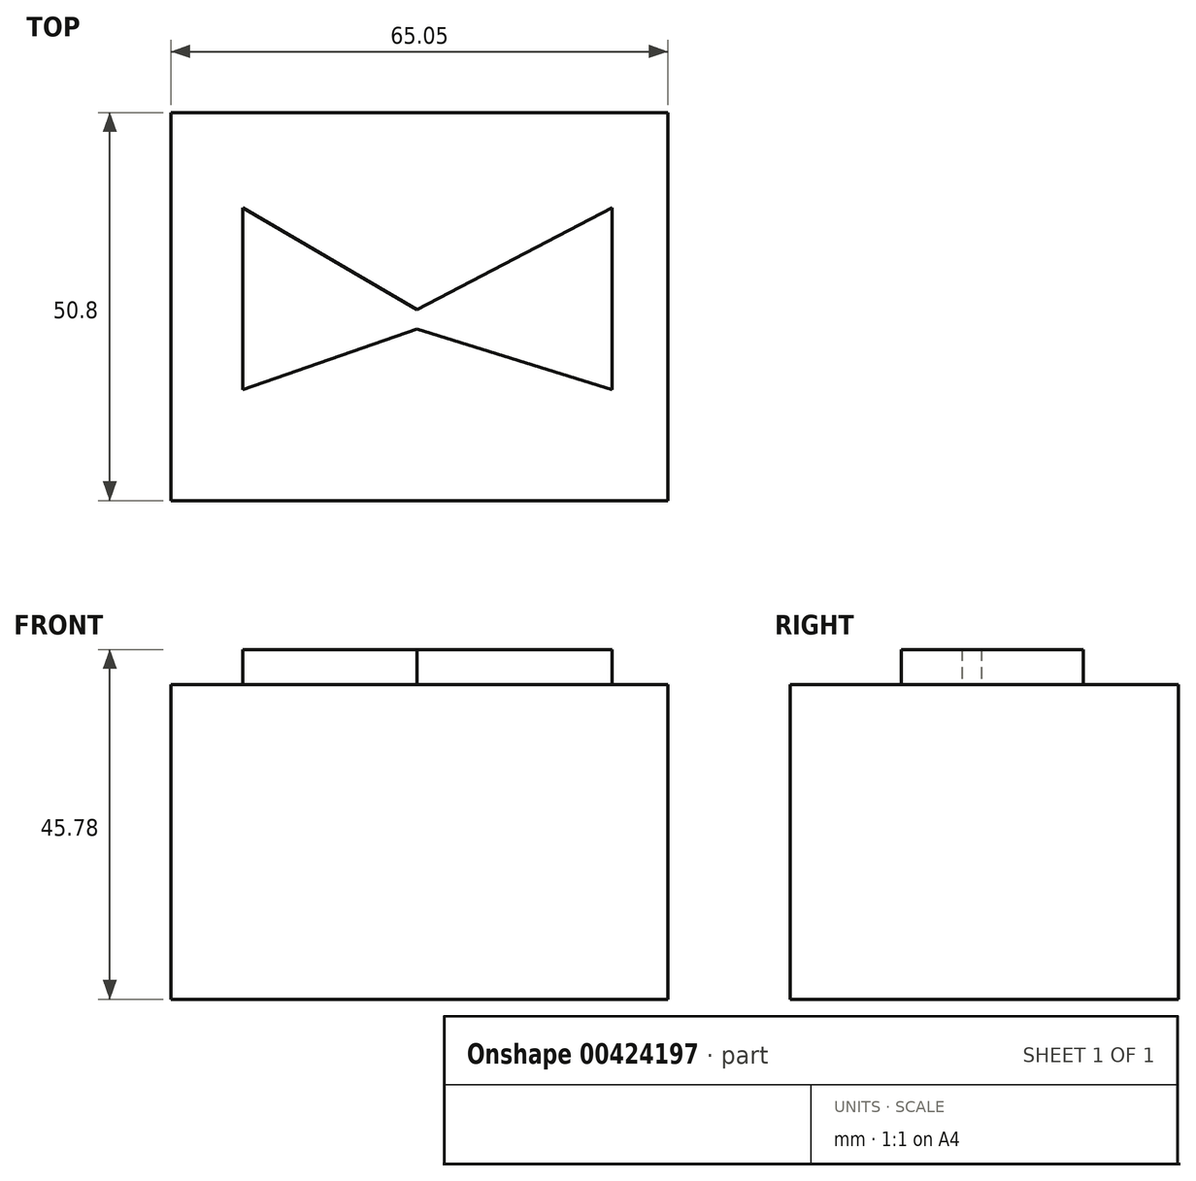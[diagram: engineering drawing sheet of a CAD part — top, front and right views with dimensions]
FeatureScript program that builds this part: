
annotation { "Feature Type Name" : "Feature", "Feature Type Description" : "" }
export const myFeature = defineFeature(function(context is Context, id is Id, definition is map)
    precondition{}
    {
        {
            var Q0;
            Q0=qCreatedBy(makeId("Front.planeOp"),FACE);
            var sketch = newSketch(context, id + "F0", { "sketchPlane" : qUnion([Q0])});
            skLineSegment(sketch, "E0.bottom", {"start": v(-32.21, 17.68) * mm, "end": v(32.84, 17.68) * mm});
            skLineSegment(sketch, "E0.top", {"start": v(-32.21, -23.53) * mm, "end": v(32.84, -23.53) * mm});
            skLineSegment(sketch, "E0.left", {"start": v(-32.21, 17.68) * mm, "end": v(-32.21, -23.53) * mm});
            skLineSegment(sketch, "E0.right", {"start": v(32.84, 17.68) * mm, "end": v(32.84, -23.53) * mm});
            skSolve(sketch);
        }
        {
            var Q0;
            Q0 = qSketchRegion(id + "F0", true);
            extrude(context, id + "F1", {"entities" : qUnion([Q0]), "depth" : 25.4 * mm});
        }
        {
            var Q0;
            Q0=makeQuery(id+"F1.opExtrude","CAP_FACE",FACE,{"disambiguationData":[OSD([sQuery(id+"F0.wireOp",EDGE,"E0.bottom"),sQuery(id+"F0.wireOp",EDGE,"E0.top"),sQuery(id+"F0.wireOp",EDGE,"E0.left"),sQuery(id+"F0.wireOp",EDGE,"E0.right")])],"isStart":false});
            var sketch = newSketch(context, id + "F2", { "sketchPlane" : qUnion([Q0])});
            skLineSegment(sketch, "E1", {"start": v(-23.43, 2.82) * mm, "end": v(-23.43, -9.1) * mm});
            skLineSegment(sketch, "E2", {"start": v(-23.43, -9.1) * mm, "end": v(0, -3.24) * mm});
            skLineSegment(sketch, "E3", {"start": v(-23.43, 2.82) * mm, "end": v(0, -3.24) * mm});
            skLineSegment(sketch, "E4", {"start": v(0, -3.24) * mm, "end": v(20.92, 2.82) * mm});
            skLineSegment(sketch, "E5", {"start": v(20.92, 2.82) * mm, "end": v(20.92, -9.1) * mm});
            skLineSegment(sketch, "E6", {"start": v(20.92, -9.1) * mm, "end": v(0, -3.24) * mm});
            skSolve(sketch);
        }
        {
            var Q0;
            Q0 = qSketchRegion(id + "F2", true);
            var Q1;
            Q1=makeQuery(id+"F2.imprint","IMPRINT",FACE,{"disambiguationData":[TD([[makeQuery(id+"F2.imprint","IMPRINT",EDGE,{"derivedFrom":sQuery(id+"F2.wireOp",EDGE,"E1")}),-1.0]])]});
            extrude(context, id + "F3", {"entities" : qUnion([Q0, Q1]), "operationType" : NewBodyOperationType.ADD, "depth" : 25.4 * mm});
        }
        {
            var Q0;
            {var subQ0=sQuery(id+"F0.wireOp",EDGE,"E0.bottom");Q0=makeQuery(id+"F3.boolean.opBoolean","MERGE",FACE,{"derivedFrom":[makeQuery(id+"F1.opExtrude","SWEPT_FACE",FACE,{"disambiguationData":[OSD([subQ0])]}),makeQuery(id+"F3.opExtrude","SWEPT_FACE",FACE,{"disambiguationData":[OSD([subQ0])]})]});}
            var sketch = newSketch(context, id + "F4", { "sketchPlane" : qUnion([Q0])});
            skLineSegment(sketch, "E7", {"start": v(-22.8, -12.45) * mm, "end": v(-22.8, -36.3) * mm});
            skLineSegment(sketch, "E8", {"start": v(25.52, -12.45) * mm, "end": v(25.52, -36.3) * mm});
            skLineSegment(sketch, "E9", {"start": v(-22.8, -12.45) * mm, "end": v(0, -25.83) * mm});
            skLineSegment(sketch, "E10", {"start": v(-22.8, -36.3) * mm, "end": v(0, -28.34) * mm});
            skLineSegment(sketch, "E11", {"start": v(0, -25.83) * mm, "end": v(25.52, -12.45) * mm});
            skLineSegment(sketch, "E12", {"start": v(0, -28.34) * mm, "end": v(25.52, -36.3) * mm});
            skSolve(sketch);
        }
        {
            var Q0;
            Q0 = qSketchRegion(id + "F4", true);
            extrude(context, id + "F5", {"entities" : qUnion([Q0]), "operationType" : NewBodyOperationType.ADD, "depth" : 4.57 * mm});
        }
    });
